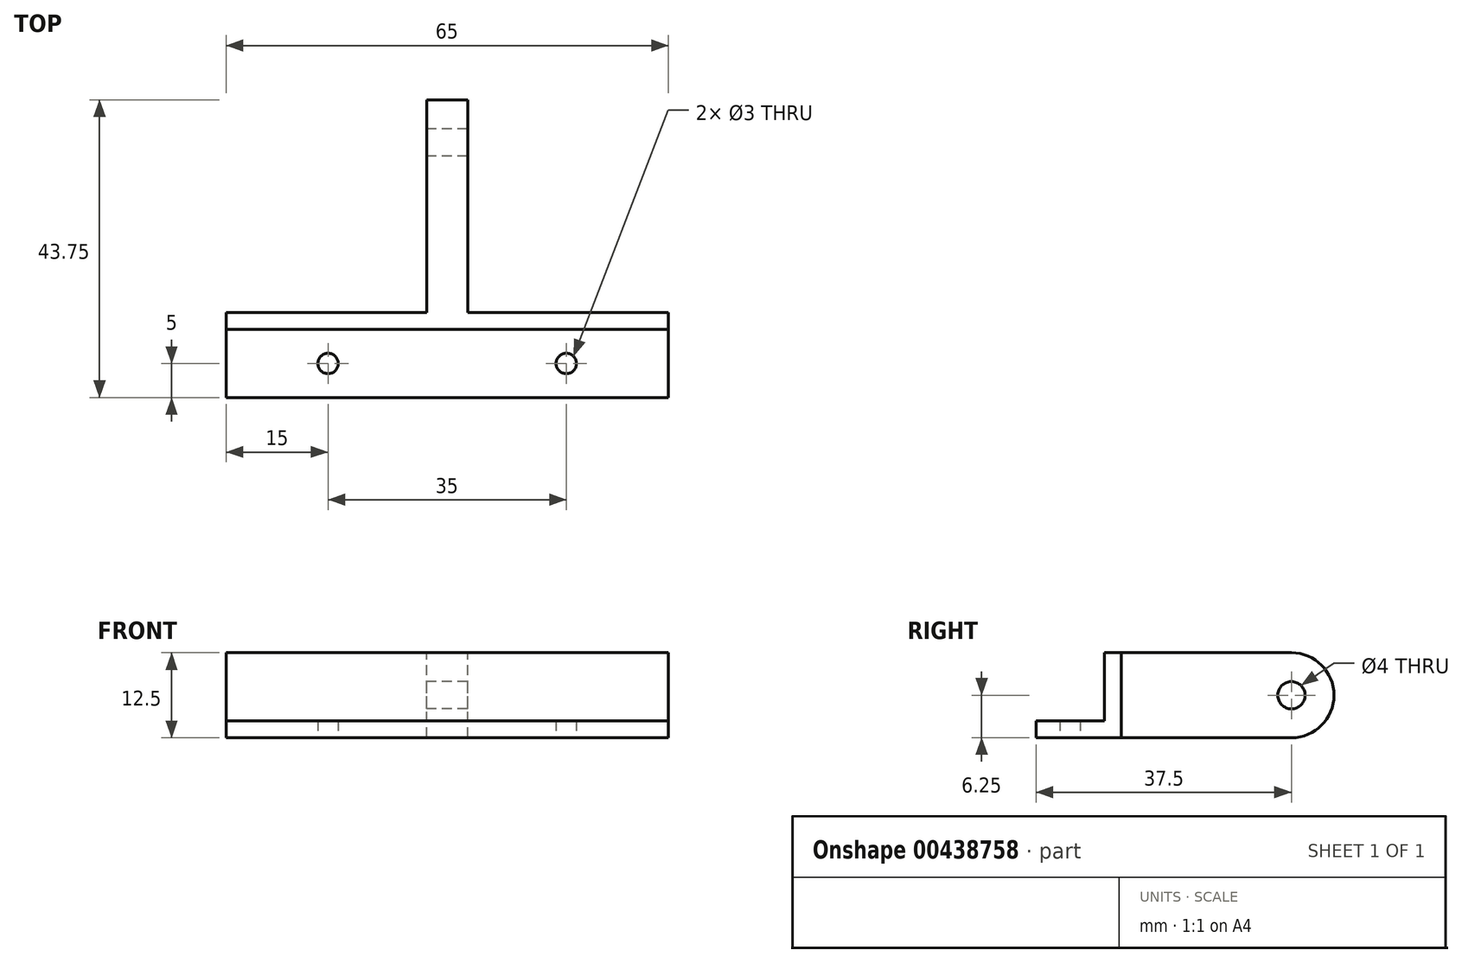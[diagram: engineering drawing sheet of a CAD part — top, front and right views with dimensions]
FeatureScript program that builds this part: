
annotation { "Feature Type Name" : "Feature", "Feature Type Description" : "" }
export const myFeature = defineFeature(function(context is Context, id is Id, definition is map)
    precondition{}
    {
        {
            var Q0;
            Q0=qCreatedBy(makeId("Top.planeOp"),FACE);
            var sketch = newSketch(context, id + "F0", { "sketchPlane" : qUnion([Q0])});
            skLineSegment(sketch, "E0.bottom", {"start": v(-32.5, 6.25) * mm, "end": v(32.5, 6.25) * mm});
            skLineSegment(sketch, "E0.top", {"start": v(-32.5, -6.25) * mm, "end": v(32.5, -6.25) * mm});
            skLineSegment(sketch, "E0.left", {"start": v(-32.5, 6.25) * mm, "end": v(-32.5, -6.25) * mm});
            skLineSegment(sketch, "E0.right", {"start": v(32.5, 6.25) * mm, "end": v(32.5, -6.25) * mm});
            skCircle(sketch, "E1", {"center": v(-17.5, -1.25) * mm, "radius": 1.5 * mm});
            skCircle(sketch, "E2.MirrorC", {"center": v(17.5, -1.25) * mm, "radius": 1.5 * mm});
            skSolve(sketch);
        }
        {
            var Q0;
            Q0 = qSketchRegion(id + "F0", true);
            extrude(context, id + "F1", {"entities" : qUnion([Q0]), "depth" : 2.5 * mm});
        }
        {
            var Q0;
            Q0=makeQuery(id+"F1.opExtrude","CAP_FACE",FACE,{"disambiguationData":[OSD([sQuery(id+"F0.wireOp",EDGE,"E0.bottom"),sQuery(id+"F0.wireOp",EDGE,"E0.top"),sQuery(id+"F0.wireOp",EDGE,"E0.left"),sQuery(id+"F0.wireOp",EDGE,"E0.right")])],"isStart":false});
            var sketch = newSketch(context, id + "F2", { "sketchPlane" : qUnion([Q0])});
            skLineSegment(sketch, "E3.bottom", {"start": v(-32.5, 6.25) * mm, "end": v(32.5, 6.25) * mm});
            skLineSegment(sketch, "E3.top", {"start": v(-32.5, 3.75) * mm, "end": v(32.5, 3.75) * mm});
            skLineSegment(sketch, "E3.left", {"start": v(-32.5, 6.25) * mm, "end": v(-32.5, 3.75) * mm});
            skLineSegment(sketch, "E3.right", {"start": v(32.5, 6.25) * mm, "end": v(32.5, 3.75) * mm});
            skSolve(sketch);
        }
        {
            var Q0;
            Q0 = qSketchRegion(id + "F2", true);
            extrude(context, id + "F3", {"entities" : qUnion([Q0]), "operationType" : NewBodyOperationType.ADD, "depth" : 10 * mm});
        }
        {
            var Q0;
            Q0=qCreatedBy(makeId("Right.planeOp"),FACE);
            var sketch = newSketch(context, id + "F4", { "sketchPlane" : qUnion([Q0])});
            skLineSegment(sketch, "E4.bottom", {"start": v(6.25, 0) * mm, "end": v(31.25, 0) * mm});
            skLineSegment(sketch, "E4.top", {"start": v(6.25, 12.5) * mm, "end": v(31.25, 12.5) * mm});
            skLineSegment(sketch, "E4.left", {"start": v(6.25, 0) * mm, "end": v(6.25, 12.5) * mm});
            skArc(sketch, "E5", {"start": v(31.25, 12.5) * mm, "mid": v(37.5, 6.25) * mm, "end": v(31.25, 0) * mm});
            skCircle(sketch, "E6", {"center": v(31.25, 6.25) * mm, "radius": 2 * mm});
            skSolve(sketch);
        }
        {
            var Q0;
            Q0 = qSketchRegion(id + "F4", true);
            extrude(context, id + "F5", {"entities" : qUnion([Q0]), "operationType" : NewBodyOperationType.ADD, "depth" : 3 * mm, "hasSecondDirection" : true, "secondDirectionOppositeDirection" : true, "secondDirectionDepth" : 3 * mm});
        }
    });
